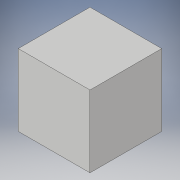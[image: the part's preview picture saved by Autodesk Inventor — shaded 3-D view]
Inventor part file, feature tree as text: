
AUTODESK INVENTOR PART (.ipt)
format: ipt  version: 2019 (Build 230136000, 136)  size: 207,872 bytes
history: native  units: mm
features: extrude x1, sketch x1
ambient origin geometry x8: Origin, YZ Plane, XZ Plane, XY Plane, X Axis, Y Axis, Z Axis, Center Point
bodies: Solid1 (feature_tree)
feature tree (2):
  extrude  "Extrusion1"  Depth=35.0mm
  sketch  "Sketch1"  dims[d0=35.0mm d1=35.0mm d2=35.0mm d3=0.0mm]
